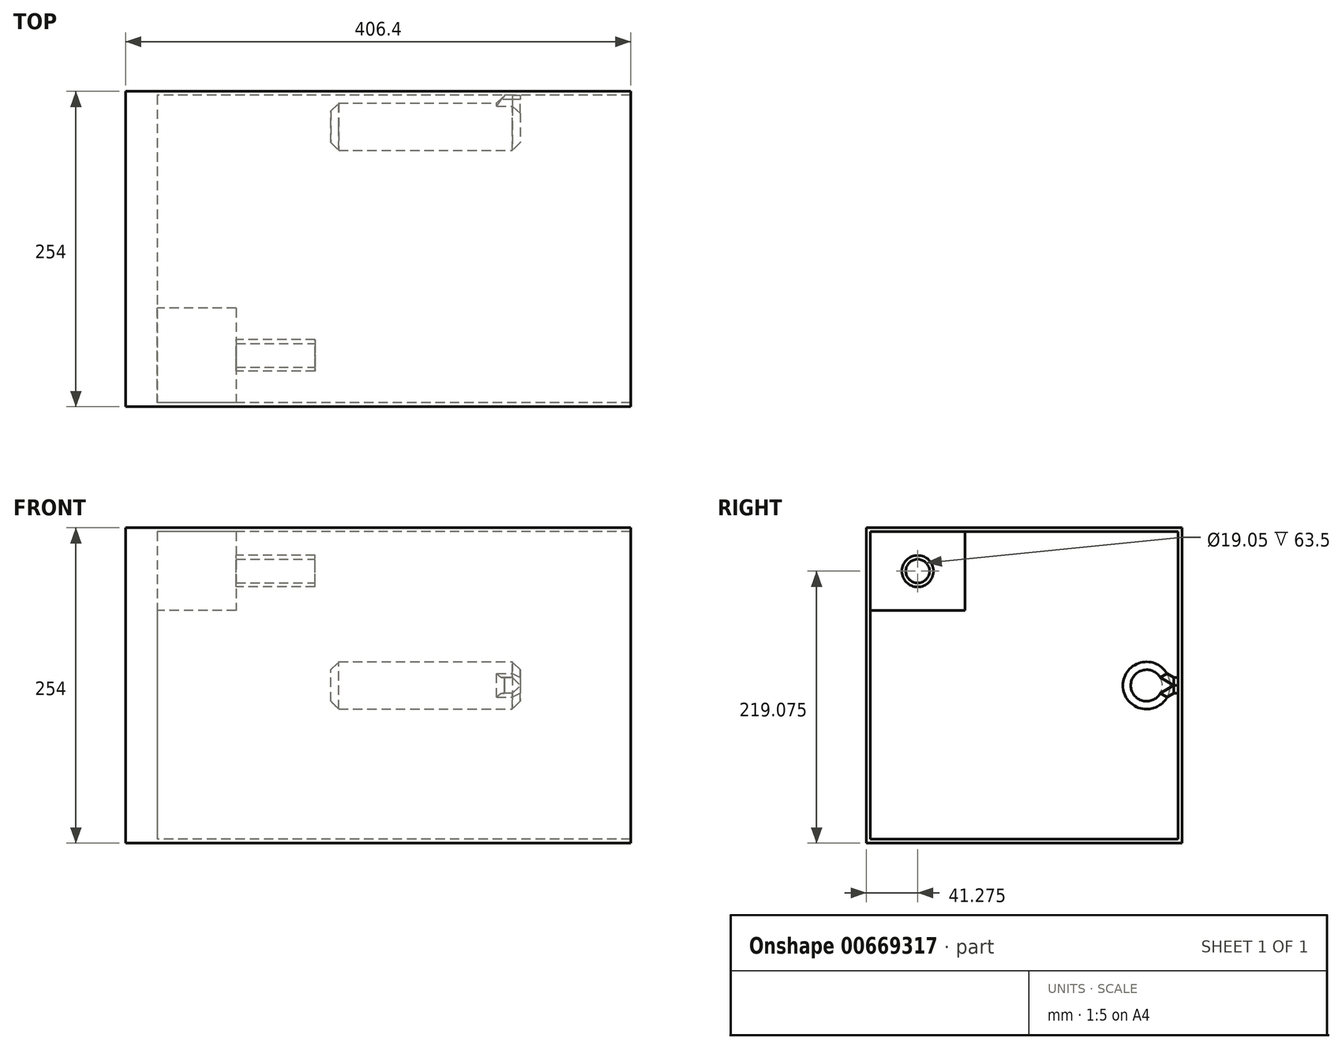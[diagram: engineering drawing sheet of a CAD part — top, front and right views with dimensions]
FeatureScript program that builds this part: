
annotation { "Feature Type Name" : "Feature", "Feature Type Description" : "" }
export const myFeature = defineFeature(function(context is Context, id is Id, definition is map)
    precondition{}
    {
        {
            var Q0;
            Q0=qCreatedBy(makeId("Right.planeOp"),FACE);
            var sketch = newSketch(context, id + "F0", { "sketchPlane" : qUnion([Q0])});
            skLineSegment(sketch, "E0.bottom", {"start": v(0, 0) * mm, "end": v(-254, 0) * mm});
            skLineSegment(sketch, "E0.top", {"start": v(0, -254) * mm, "end": v(-254, -254) * mm});
            skLineSegment(sketch, "E0.left", {"start": v(0, 0) * mm, "end": v(0, -254) * mm});
            skLineSegment(sketch, "E0.right", {"start": v(-254, 0) * mm, "end": v(-254, -254) * mm});
            skSolve(sketch);
        }
        {
            var Q0;
            Q0=makeQuery(id+"F0.imprint","IMPRINT",FACE,{"disambiguationData":[TD([[makeQuery(id+"F0.imprint","IMPRINT",EDGE,{"derivedFrom":sQuery(id+"F0.wireOp",EDGE,"E0.bottom")}),1.0]])]});
            extrude(context, id + "F1", {"entities" : qUnion([Q0]), "depth" : 25.4 * mm, "offsetDistance" : 25.4 * mm});
        }
        {
            var Q0;
            Q0=makeQuery(id+"F1.opExtrude","CAP_FACE",FACE,{"disambiguationData":[OSD([sQuery(id+"F0.wireOp",EDGE,"E0.bottom"),sQuery(id+"F0.wireOp",EDGE,"E0.top"),sQuery(id+"F0.wireOp",EDGE,"E0.left"),sQuery(id+"F0.wireOp",EDGE,"E0.right")])],"isStart":false});
            var sketch = newSketch(context, id + "F2", { "sketchPlane" : qUnion([Q0])});
            skLineSegment(sketch, "E1", {"start": v(-254, 0) * mm, "end": v(0, -254) * mm});
            skLineSegment(sketch, "E2.bottom", {"start": v(-3.17, -3.17) * mm, "end": v(-250.82, -3.17) * mm});
            skLineSegment(sketch, "E2.top", {"start": v(-3.18, -250.82) * mm, "end": v(-250.83, -250.82) * mm});
            skLineSegment(sketch, "E2.left", {"start": v(-3.17, -3.17) * mm, "end": v(-3.18, -250.83) * mm});
            skLineSegment(sketch, "E2.right", {"start": v(-250.82, -3.17) * mm, "end": v(-250.83, -250.82) * mm});
            skPoint(sketch, "E2.middle", {"position": v(-127, -127) * mm});
            skSolve(sketch);
        }
        {
            var Q0;
            {var subQ1=sQuery(id+"F2.wireOp",EDGE,"E2.top");Q0=makeQuery(id+"F2.imprint","IMPRINT",FACE,{"disambiguationData":[TD([[makeQuery(id+"F2.imprint","IMPRINT",EDGE,{"derivedFrom":subQ1}),1.0]])]});}
            var Q1;
            {var subQ0=sQuery(id+"F2.wireOp",EDGE,"E2.bottom");Q1=makeQuery(id+"F2.imprint","IMPRINT",FACE,{"disambiguationData":[TD([[makeQuery(id+"F2.imprint","IMPRINT",EDGE,{"derivedFrom":subQ0}),-1.0]])]});}
            extrude(context, id + "F3", {"entities" : qUnion([Q0, Q1]), "operationType" : NewBodyOperationType.ADD, "depth" : 381 * mm, "offsetDistance" : 25.4 * mm});
        }
        {
            var Q0;
            Q0=makeQuery(id+"F3.opExtrude","SWEPT_FACE",FACE,{"disambiguationData":[OSD([sQuery(id+"F2.wireOp",EDGE,"E2.left")])]});
            var sketch = newSketch(context, id + "F4", { "sketchPlane" : qUnion([Q0])});
            skLineSegment(sketch, "E3", {"start": v(25.4, -3.17) * mm, "end": v(25.4, -250.82) * mm});
            skLineSegment(sketch, "E4", {"start": v(25.4, -250.82) * mm, "end": v(25.4, -127) * mm});
            skLineSegment(sketch, "E5", {"start": v(25.4, -127) * mm, "end": v(406.4, -127) * mm});
            skLineSegment(sketch, "E6", {"start": v(406.4, -127) * mm, "end": v(215.9, -127) * mm});
            skLineSegment(sketch, "E7", {"start": v(215.9, -127) * mm, "end": v(311.15, -127) * mm});
            skLineSegment(sketch, "E8.bottom", {"start": v(317.5, -120.65) * mm, "end": v(304.8, -120.65) * mm});
            skLineSegment(sketch, "E8.top", {"start": v(317.5, -133.35) * mm, "end": v(304.8, -133.35) * mm});
            skLineSegment(sketch, "E8.left", {"start": v(317.5, -120.65) * mm, "end": v(317.5, -133.35) * mm});
            skLineSegment(sketch, "E8.right", {"start": v(304.8, -120.65) * mm, "end": v(304.8, -133.35) * mm});
            skPoint(sketch, "E8.middle", {"position": v(311.15, -127) * mm});
            skSolve(sketch);
        }
        {
            var Q0;
            Q0 = qSketchRegion(id + "F4", true);
            extrude(context, id + "F5", {"entities" : qUnion([Q0]), "operationType" : NewBodyOperationType.ADD, "depth" : 25.4 * mm, "offsetDistance" : 25.4 * mm});
        }
        {
            var Q0;
            Q0=makeQuery(id+"F1.opExtrude","CAP_FACE",FACE,{"disambiguationData":[OSD([sQuery(id+"F0.wireOp",EDGE,"E0.bottom"),sQuery(id+"F0.wireOp",EDGE,"E0.top"),sQuery(id+"F0.wireOp",EDGE,"E0.left"),sQuery(id+"F0.wireOp",EDGE,"E0.right")])],"isStart":false});
            var sketch = newSketch(context, id + "F6", { "sketchPlane" : qUnion([Q0])});
            skLineSegment(sketch, "E9.bottom", {"start": v(-23.55, -77.41) * mm, "end": v(-11.44, -77.41) * mm});
            skLineSegment(sketch, "E9.top", {"start": v(-23.55, -189.47) * mm, "end": v(-11.44, -189.47) * mm});
            skLineSegment(sketch, "E9.left", {"start": v(-23.55, -77.41) * mm, "end": v(-23.55, -189.47) * mm});
            skLineSegment(sketch, "E9.right", {"start": v(-11.44, -77.41) * mm, "end": v(-11.44, -189.47) * mm});
            skPoint(sketch, "E9.middle", {"position": v(-17.5, -133.44) * mm});
            skSolve(sketch);
        }
        {
            var Q0;
            Q0=makeQuery(id+"F6.imprint","IMPRINT",FACE,{"disambiguationData":[TD([[makeQuery(id+"F6.imprint","IMPRINT",EDGE,{"derivedFrom":sQuery(id+"F6.wireOp",EDGE,"E9.bottom")}),-1.0]])]});
            extrude(context, id + "F7", {"entities" : qUnion([Q0]), "operationType" : NewBodyOperationType.REMOVE, "oppositeDirection" : true, "depth" : 25.4 * mm, "offsetDistance" : 25.4 * mm});
        }
        {
            var Q0;
            Q0=makeQuery(id+"F5.opExtrude","SWEPT_FACE",FACE,{"disambiguationData":[OSD([sQuery(id+"F4.wireOp",EDGE,"E8.left")])]});
            var sketch = newSketch(context, id + "F8", { "sketchPlane" : qUnion([Q0])});
            skCircle(sketch, "E10", {"center": v(-28.57, -127) * mm, "radius": 19.05 * mm});
            skSolve(sketch);
        }
        {
            var Q0;
            Q0 = qSketchRegion(id + "F8", true);
            extrude(context, id + "F9", {"entities" : qUnion([Q0]), "operationType" : NewBodyOperationType.ADD, "oppositeDirection" : true, "depth" : 152.4 * mm, "offsetDistance" : 25.4 * mm});
        }
        {
            var Q0;
            Q0=makeQuery(id+"F1.opExtrude","CAP_FACE",FACE,{"disambiguationData":[OSD([sQuery(id+"F0.wireOp",EDGE,"E0.bottom"),sQuery(id+"F0.wireOp",EDGE,"E0.top"),sQuery(id+"F0.wireOp",EDGE,"E0.left"),sQuery(id+"F0.wireOp",EDGE,"E0.right")])],"isStart":false});
            var sketch = newSketch(context, id + "F10", { "sketchPlane" : qUnion([Q0])});
            skLineSegment(sketch, "E11.bottom", {"start": v(-23.55, -77.41) * mm, "end": v(-11.44, -77.41) * mm});
            skLineSegment(sketch, "E11.top", {"start": v(-23.55, -189.47) * mm, "end": v(-11.44, -189.47) * mm});
            skLineSegment(sketch, "E11.left", {"start": v(-23.55, -77.41) * mm, "end": v(-23.55, -189.47) * mm});
            skLineSegment(sketch, "E11.right", {"start": v(-11.44, -77.41) * mm, "end": v(-11.44, -189.47) * mm});
            skSolve(sketch);
        }
        {
            var Q0;
            Q0 = qSketchRegion(id + "F10", true);
            extrude(context, id + "F11", {"entities" : qUnion([Q0]), "operationType" : NewBodyOperationType.ADD, "oppositeDirection" : true, "depth" : 25.4 * mm, "offsetDistance" : 25.4 * mm});
        }
        {
            var Q0;
            Q0=makeQuery(id+"F9.opExtrude","SWEPT_FACE",FACE,{"disambiguationData":[OSD([sQuery(id+"F8.wireOp",EDGE,"E10")])]});
            chamfer(context, id + "F12", {"entities" : qUnion([Q0]), "width" : 6.35 * mm, "tangentPropagation" : true});
        }
        {
            var Q0;
            Q0=makeQuery(id+"F11.boolean.opBoolean","MERGE",FACE,{"derivedFrom":[makeQuery(id+"F1.opExtrude","CAP_FACE",FACE,{"disambiguationData":[OSD([sQuery(id+"F0.wireOp",EDGE,"E0.bottom"),sQuery(id+"F0.wireOp",EDGE,"E0.top"),sQuery(id+"F0.wireOp",EDGE,"E0.left"),sQuery(id+"F0.wireOp",EDGE,"E0.right")])],"isStart":false}),makeQuery(id+"F11.opExtrude","CAP_FACE",FACE,{"disambiguationData":[OSD([sQuery(id+"F10.wireOp",EDGE,"E11.bottom"),sQuery(id+"F10.wireOp",EDGE,"E11.top"),sQuery(id+"F10.wireOp",EDGE,"E11.left"),sQuery(id+"F10.wireOp",EDGE,"E11.right")])],"isStart":true})]});
            var sketch = newSketch(context, id + "F13", { "sketchPlane" : qUnion([Q0])});
            skLineSegment(sketch, "E12.bottom", {"start": v(-250.82, -3.18) * mm, "end": v(-174.62, -3.18) * mm});
            skLineSegment(sketch, "E12.top", {"start": v(-250.82, -66.68) * mm, "end": v(-174.62, -66.68) * mm});
            skLineSegment(sketch, "E12.left", {"start": v(-250.82, -3.18) * mm, "end": v(-250.82, -66.68) * mm});
            skLineSegment(sketch, "E12.right", {"start": v(-174.62, -3.18) * mm, "end": v(-174.62, -66.68) * mm});
            skSolve(sketch);
        }
        {
            var Q0;
            Q0 = qSketchRegion(id + "F13", true);
            extrude(context, id + "F14", {"entities" : qUnion([Q0]), "operationType" : NewBodyOperationType.ADD, "depth" : 63.5 * mm, "offsetDistance" : 25.4 * mm});
        }
        {
            var Q0;
            Q0=makeQuery(id+"F14.opExtrude","CAP_FACE",FACE,{"disambiguationData":[OSD([sQuery(id+"F13.wireOp",EDGE,"E12.bottom"),sQuery(id+"F13.wireOp",EDGE,"E12.top"),sQuery(id+"F13.wireOp",EDGE,"E12.left"),sQuery(id+"F13.wireOp",EDGE,"E12.right")])],"isStart":false});
            var sketch = newSketch(context, id + "F15", { "sketchPlane" : qUnion([Q0])});
            skLineSegment(sketch, "E13", {"start": v(-250.83, -66.68) * mm, "end": v(-174.62, -3.17) * mm});
            skCircle(sketch, "E14", {"center": v(-212.72, -34.93) * mm, "radius": 12.7 * mm});
            skSolve(sketch);
        }
        {
            var Q0;
            Q0 = qSketchRegion(id + "F15", true);
            extrude(context, id + "F16", {"entities" : qUnion([Q0]), "operationType" : NewBodyOperationType.ADD, "depth" : 63.5 * mm, "offsetDistance" : 25.4 * mm});
        }
        {
            var Q0;
            Q0=makeQuery(id+"F16.opExtrude","CAP_FACE",FACE,{"disambiguationData":[OSD([sQuery(id+"F15.wireOp",EDGE,"E14")])],"isStart":false});
            var sketch = newSketch(context, id + "F17", { "sketchPlane" : qUnion([Q0])});
            skCircle(sketch, "E15", {"center": v(-212.72, -34.93) * mm, "radius": 9.53 * mm});
            skSolve(sketch);
        }
        {
            var Q0;
            Q0=makeQuery(id+"F17.imprint","IMPRINT",FACE,{"disambiguationData":[TD([[makeQuery(id+"F17.imprint","IMPRINT",EDGE,{"derivedFrom":sQuery(id+"F17.wireOp",EDGE,"E15")}),1.0]])]});
            extrude(context, id + "F18", {"entities" : qUnion([Q0]), "operationType" : NewBodyOperationType.REMOVE, "oppositeDirection" : true, "depth" : 63.5 * mm, "offsetDistance" : 25.4 * mm});
        }
    });
